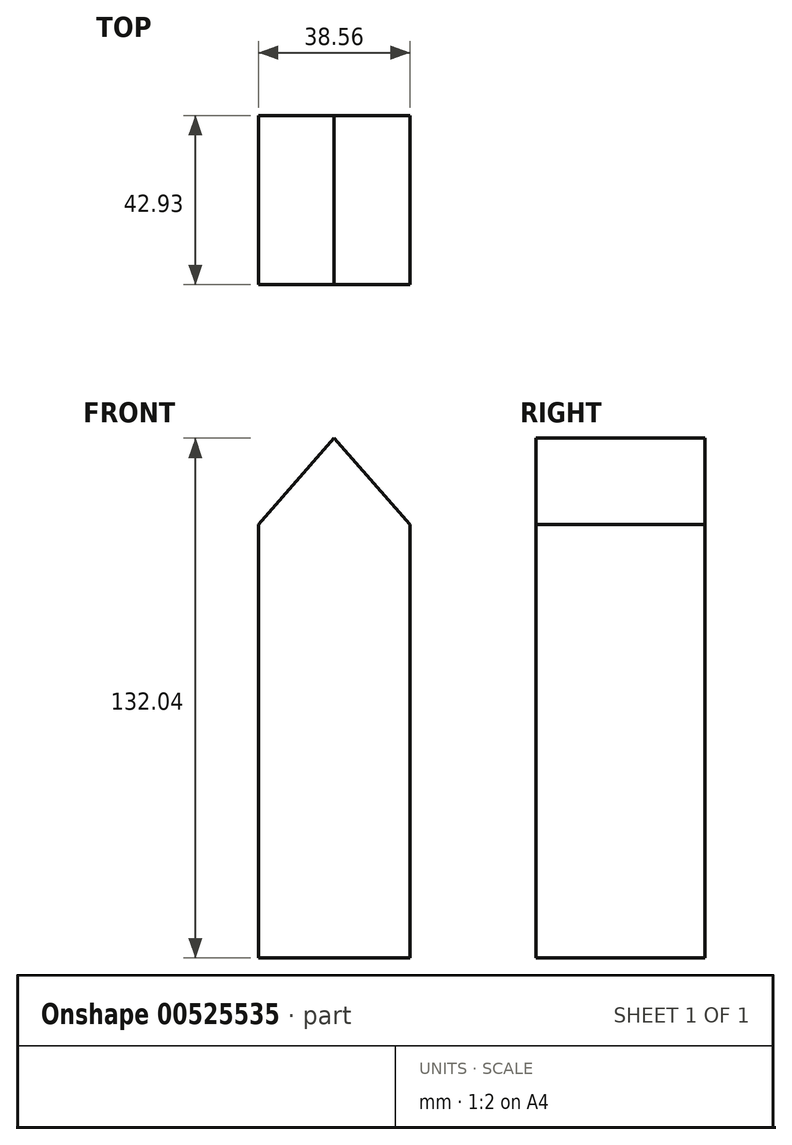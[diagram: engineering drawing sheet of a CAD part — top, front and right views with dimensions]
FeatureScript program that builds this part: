
annotation { "Feature Type Name" : "Feature", "Feature Type Description" : "" }
export const myFeature = defineFeature(function(context is Context, id is Id, definition is map)
    precondition{}
    {
        {
            var Q0;
            Q0=qCreatedBy(makeId("Front.planeOp"),FACE);
            var sketch = newSketch(context, id + "F0", { "sketchPlane" : qUnion([Q0])});
            skLineSegment(sketch, "E0.bottom", {"start": v(-19.28, 55.04) * mm, "end": v(19.28, 55.04) * mm});
            skLineSegment(sketch, "E0.top", {"start": v(-19.28, -55.04) * mm, "end": v(19.28, -55.04) * mm});
            skLineSegment(sketch, "E0.left", {"start": v(-19.28, 55.04) * mm, "end": v(-19.28, -55.04) * mm});
            skLineSegment(sketch, "E0.right", {"start": v(19.28, 55.04) * mm, "end": v(19.28, -55.04) * mm});
            skPoint(sketch, "E0.middle", {"position": v(0, 0) * mm});
            skLineSegment(sketch, "E1", {"start": v(-19.28, 55.04) * mm, "end": v(0, 77) * mm});
            skLineSegment(sketch, "E2", {"start": v(0, 77) * mm, "end": v(19.28, 55.04) * mm});
            skSolve(sketch);
        }
        {
            var Q0;
            Q0 = qSketchRegion(id + "F0", true);
            extrude(context, id + "F1", {"entities" : qUnion([Q0]), "depth" : 42.93 * mm, "offsetDistance" : 25.4 * mm});
        }
    });
